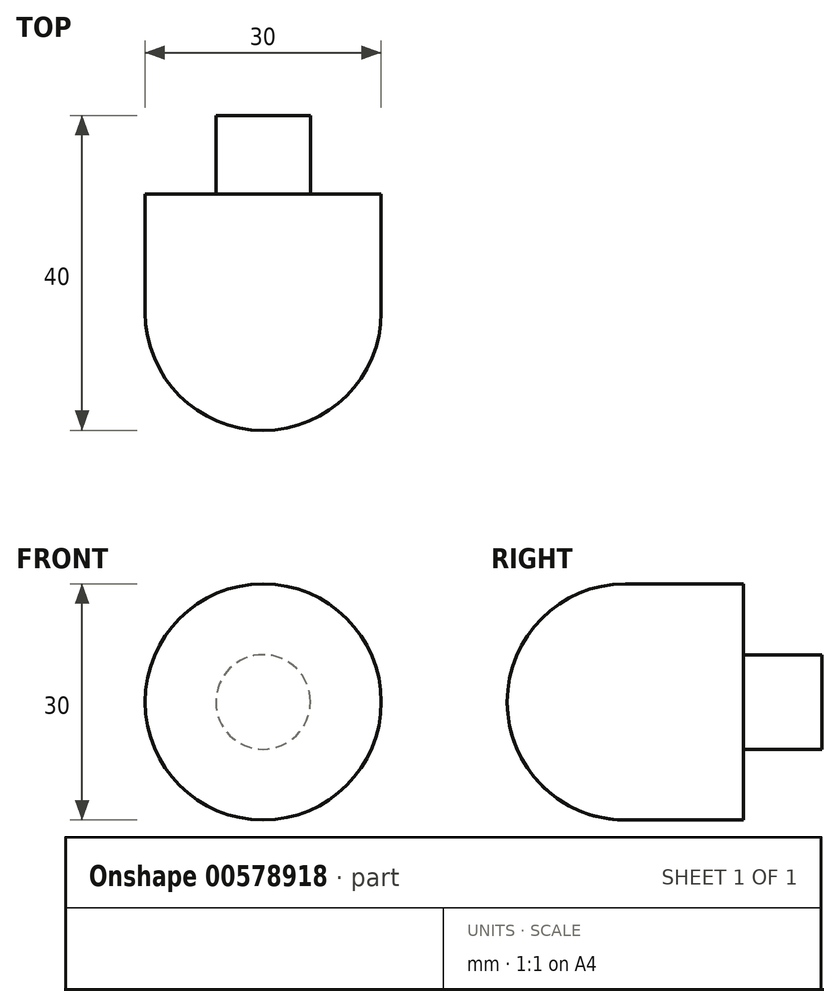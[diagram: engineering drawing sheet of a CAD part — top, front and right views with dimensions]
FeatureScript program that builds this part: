
annotation { "Feature Type Name" : "Feature", "Feature Type Description" : "" }
export const myFeature = defineFeature(function(context is Context, id is Id, definition is map)
    precondition{}
    {
        {
            var Q0;
            Q0=qCreatedBy(makeId("Front.planeOp"),FACE);
            var sketch = newSketch(context, id + "F0", { "sketchPlane" : qUnion([Q0])});
            skCircle(sketch, "E0", {"center": v(0, 0) * mm, "radius": 6 * mm});
            skSolve(sketch);
        }
        {
            var Q0;
            Q0 = qSketchRegion(id + "F0", true);
            extrude(context, id + "F1", {"entities" : qUnion([Q0]), "depth" : 10 * mm, "offsetDistance" : 25 * mm});
        }
        {
            var Q0;
            Q0=makeQuery(id+"F1.opExtrude","CAP_FACE",FACE,{"disambiguationData":[OSD([sQuery(id+"F0.wireOp",EDGE,"E0")])],"isStart":false});
            var sketch = newSketch(context, id + "F2", { "sketchPlane" : qUnion([Q0])});
            skCircle(sketch, "E1", {"center": v(0, 0) * mm, "radius": 15 * mm});
            skSolve(sketch);
        }
        {
            var Q0;
            Q0 = qSketchRegion(id + "F2", true);
            extrude(context, id + "F3", {"entities" : qUnion([Q0]), "operationType" : NewBodyOperationType.ADD, "depth" : 30 * mm, "offsetDistance" : 25 * mm});
        }
        {
            var Q0;
            Q0=makeQuery(id+"F3.opExtrude","CAP_FACE",FACE,{"disambiguationData":[OSD([sQuery(id+"F2.wireOp",EDGE,"E1")])],"isStart":false});
            fillet(context, id + "F4", {"entities" : qUnion([Q0]), "radius" : 15 * mm, "tangentPropagation" : true, "allowEdgeOverflow" : false});
        }
    });
